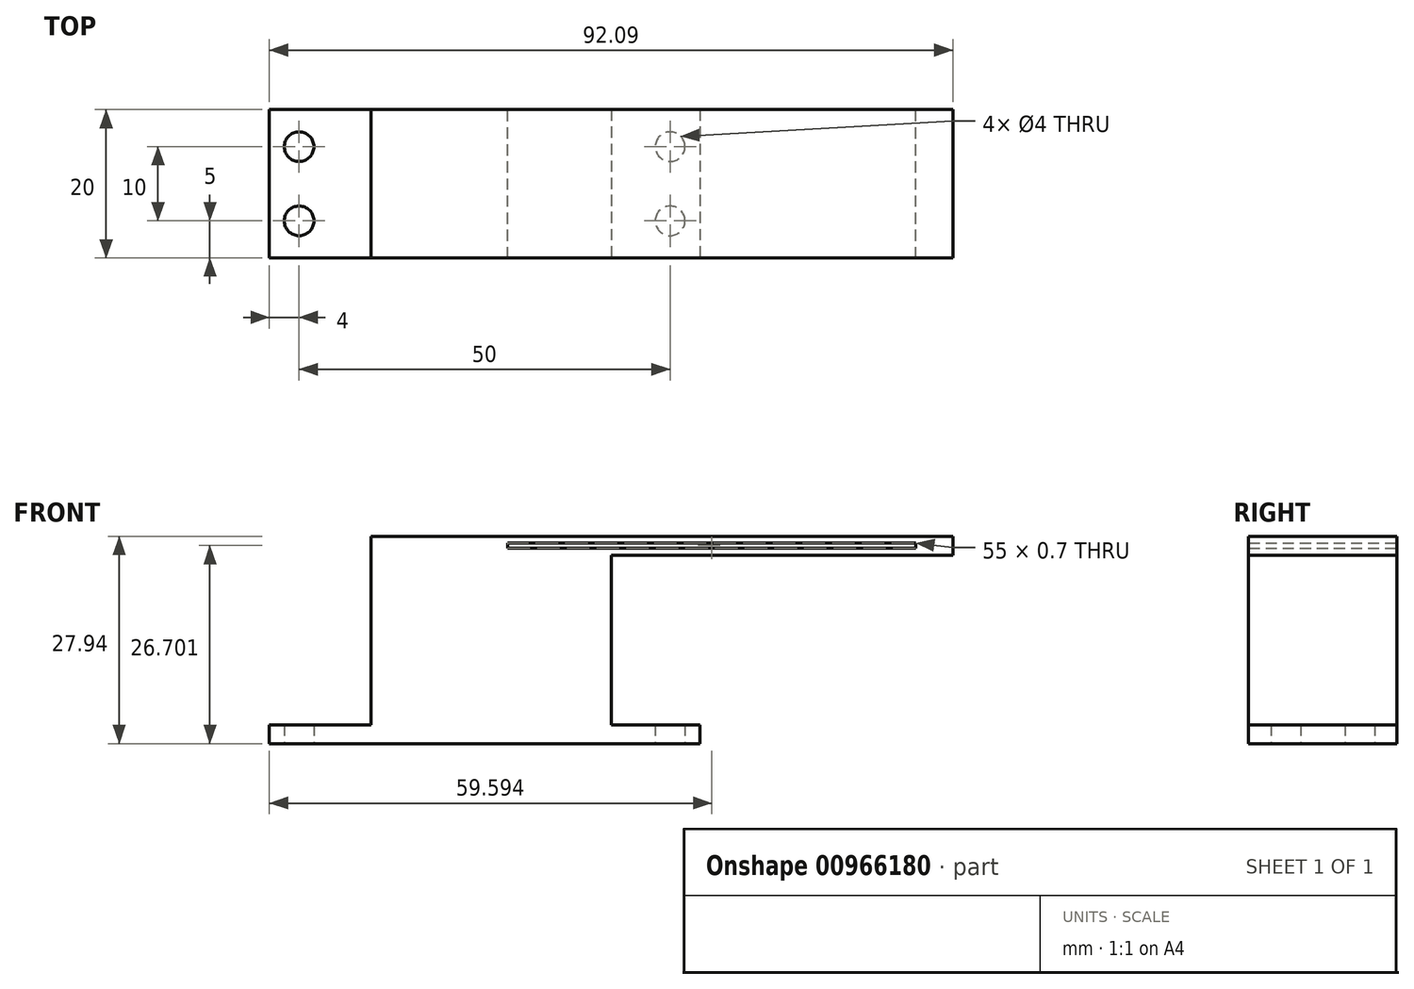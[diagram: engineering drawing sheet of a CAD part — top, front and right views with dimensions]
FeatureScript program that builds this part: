
annotation { "Feature Type Name" : "Feature", "Feature Type Description" : "" }
export const myFeature = defineFeature(function(context is Context, id is Id, definition is map)
    precondition{}
    {
        {
            var Q0;
            Q0=qCreatedBy(makeId("Top.planeOp"),FACE);
            var sketch = newSketch(context, id + "F0", { "sketchPlane" : qUnion([Q0])});
            skLineSegment(sketch, "E0.bottom", {"start": v(-29, 10) * mm, "end": v(29, 10) * mm});
            skLineSegment(sketch, "E0.top", {"start": v(-29, -10) * mm, "end": v(29, -10) * mm});
            skLineSegment(sketch, "E0.left", {"start": v(-29, 10) * mm, "end": v(-29, -10) * mm});
            skLineSegment(sketch, "E0.right", {"start": v(29, 10) * mm, "end": v(29, -10) * mm});
            skCircle(sketch, "E1", {"center": v(-25, 5) * mm, "radius": 2 * mm});
            skCircle(sketch, "E2", {"center": v(-25, -5) * mm, "radius": 2 * mm});
            skCircle(sketch, "E3", {"center": v(25, 5) * mm, "radius": 2 * mm});
            skCircle(sketch, "E4", {"center": v(25, -5) * mm, "radius": 2 * mm});
            skSolve(sketch);
        }
        {
            var Q0;
            Q0=qSketchRegion(id+"F0",true);
            extrude(context, id + "F1", {"entities" : qUnion([Q0]), "depth" : 2.54 * mm, "offsetDistance" : 25.4 * mm});
        }
        {
            var Q0;
            Q0=makeQuery(id+"F1.opExtrude","CAP_FACE",FACE,{"disambiguationData":[OSD([sQuery(id+"F0.wireOp",EDGE,"747ac24a-afe5-4b64-999f-19a3d27787b8"),sQuery(id+"F0.wireOp",EDGE,"5c8f7829-6496-412c-866f-dbe53b567064"),sQuery(id+"F0.wireOp",EDGE,"ef2c8e1f-5198-447a-a13a-cbf40e058c80"),sQuery(id+"F0.wireOp",EDGE,"5ca80856-a312-4663-bb65-8766e3786a1f"),sQuery(id+"F0.wireOp",EDGE,"E0.bottom"),sQuery(id+"F0.wireOp",EDGE,"E0.top"),sQuery(id+"F0.wireOp",EDGE,"E0.left"),sQuery(id+"F0.wireOp",EDGE,"E0.right")])],"isStart":false});
            var sketch = newSketch(context, id + "F2", { "sketchPlane" : qUnion([Q0])});
            skLineSegment(sketch, "E5.bottom", {"start": v(-15.3, 10) * mm, "end": v(17.1, 10) * mm});
            skLineSegment(sketch, "E5.top", {"start": v(-15.3, -10) * mm, "end": v(17.1, -10) * mm});
            skLineSegment(sketch, "E5.left", {"start": v(-15.3, 10) * mm, "end": v(-15.3, -10) * mm});
            skLineSegment(sketch, "E5.right", {"start": v(17.1, 10) * mm, "end": v(17.1, -10) * mm});
            skSolve(sketch);
        }
        {
            var Q0;
            Q0=makeQuery(id+"F2.imprint","IMPRINT",FACE,{"disambiguationData":[TD([[makeQuery(id+"F2.imprint","IMPRINT",EDGE,{"derivedFrom":sQuery(id+"F2.wireOp",EDGE,"E5.bottom")}),-1.0]])]});
            extrude(context, id + "F3", {"entities" : qUnion([Q0]), "operationType" : NewBodyOperationType.ADD, "depth" : 25.4 * mm, "offsetDistance" : 25.4 * mm});
        }
        {
            var Q0;
            Q0=makeQuery(id+"F3.opExtrude","SWEPT_FACE",FACE,{"disambiguationData":[OSD([sQuery(id+"F2.wireOp",EDGE,"E5.right")])]});
            var sketch = newSketch(context, id + "F4", { "sketchPlane" : qUnion([Q0])});
            skLineSegment(sketch, "E6.bottom", {"start": v(10, 27.94) * mm, "end": v(-10, 27.94) * mm});
            skLineSegment(sketch, "E6.top", {"start": v(10, 25.4) * mm, "end": v(-10, 25.4) * mm});
            skLineSegment(sketch, "E6.left", {"start": v(10, 27.94) * mm, "end": v(10, 25.4) * mm});
            skLineSegment(sketch, "E6.right", {"start": v(-10, 27.94) * mm, "end": v(-10, 25.4) * mm});
            skSolve(sketch);
        }
        {
            var Q0;
            Q0=makeQuery(id+"F4.imprint","IMPRINT",FACE,{"disambiguationData":[TD([[makeQuery(id+"F4.imprint","IMPRINT",EDGE,{"derivedFrom":sQuery(id+"F4.wireOp",EDGE,"E6.bottom")}),1.0]])]});
            extrude(context, id + "F5", {"entities" : qUnion([Q0]), "operationType" : NewBodyOperationType.ADD, "depth" : 46 * mm, "offsetDistance" : 25.4 * mm});
        }
        {
            var Q0;
            Q0=makeQuery(id+"F5.boolean.opBoolean","MERGE",FACE,{"derivedFrom":[makeQuery(id+"F3.boolean.opBoolean","MERGE",FACE,{"derivedFrom":[makeQuery(id+"F1.opExtrude","SWEPT_FACE",FACE,{"disambiguationData":[OSD([sQuery(id+"F0.wireOp",EDGE,"E0.bottom")])]}),makeQuery(id+"F3.opExtrude","SWEPT_FACE",FACE,{"disambiguationData":[OSD([sQuery(id+"F2.wireOp",EDGE,"E5.bottom")])]})]}),makeQuery(id+"F5.opExtrude","SWEPT_FACE",FACE,{"disambiguationData":[OSD([sQuery(id+"F4.wireOp",EDGE,"E6.left")])]})]});
            var sketch = newSketch(context, id + "F6", { "sketchPlane" : qUnion([Q0])});
            skLineSegment(sketch, "E7.bottom", {"start": v(-58.1, 27.05) * mm, "end": v(-3.1, 27.05) * mm});
            skLineSegment(sketch, "E7.top", {"start": v(-58.1, 26.35) * mm, "end": v(-3.1, 26.35) * mm});
            skLineSegment(sketch, "E7.left", {"start": v(-58.1, 27.05) * mm, "end": v(-58.1, 26.35) * mm});
            skLineSegment(sketch, "E7.right", {"start": v(-3.1, 27.05) * mm, "end": v(-3.1, 26.35) * mm});
            skSolve(sketch);
        }
        {
            var Q0;
            Q0=makeQuery(id+"F6.imprint","IMPRINT",FACE,{"disambiguationData":[TD([[makeQuery(id+"F6.imprint","IMPRINT",EDGE,{"derivedFrom":sQuery(id+"F6.wireOp",EDGE,"E7.bottom")}),-1.0]])]});
            extrude(context, id + "F7", {"entities" : qUnion([Q0]), "operationType" : NewBodyOperationType.REMOVE, "endBound" : BoundingType.THROUGH_ALL, "oppositeDirection" : true, "depth" : 25.4 * mm, "offsetDistance" : 25.4 * mm});
        }
    });
